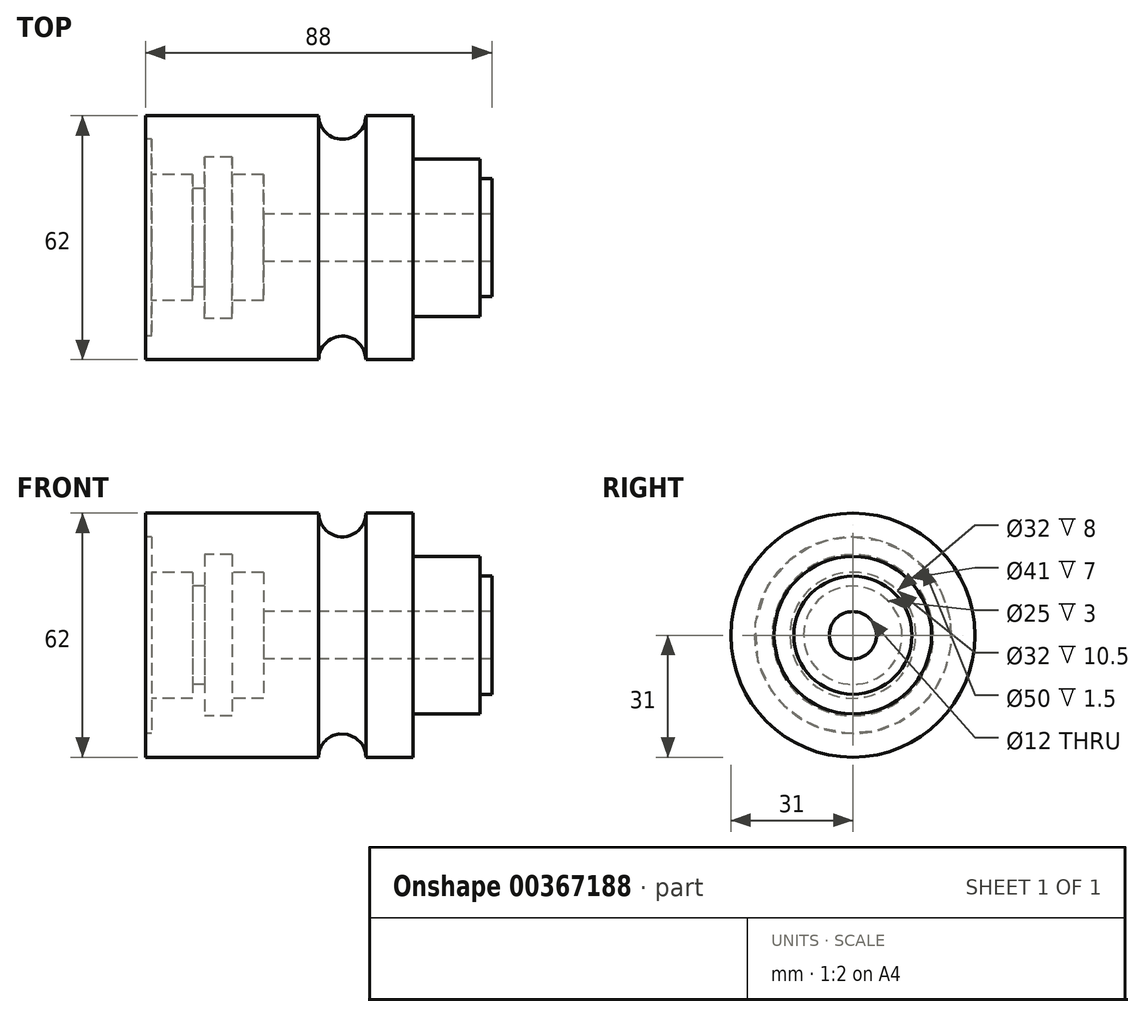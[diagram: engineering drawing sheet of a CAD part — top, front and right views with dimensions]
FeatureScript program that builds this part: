
annotation { "Feature Type Name" : "Feature", "Feature Type Description" : "" }
export const myFeature = defineFeature(function(context is Context, id is Id, definition is map)
    precondition{}
    {
        {
            var Q0;
            Q0=qCreatedBy(makeId("Front.planeOp"),FACE);
            var sketch = newSketch(context, id + "F0", { "sketchPlane" : qUnion([Q0])});
            skLineSegment(sketch, "E0", {"start": v(0, 0) * mm, "end": v(178.14, 0) * mm, "construction": true});
            skLineSegment(sketch, "E1", {"start": v(0, 0) * mm, "end": v(0, 31) * mm});
            skLineSegment(sketch, "E2", {"start": v(0, 31) * mm, "end": v(44, 31) * mm});
            skLineSegment(sketch, "E3", {"start": v(68, 31) * mm, "end": v(68, 20) * mm});
            skLineSegment(sketch, "E4", {"start": v(88, 15) * mm, "end": v(88, 0) * mm});
            skLineSegment(sketch, "E5", {"start": v(88, 0) * mm, "end": v(0, 0) * mm});
            skLineSegment(sketch, "E6", {"start": v(68, 20) * mm, "end": v(85, 20) * mm});
            skLineSegment(sketch, "E7", {"start": v(85, 20) * mm, "end": v(85, 15) * mm});
            skLineSegment(sketch, "E8", {"start": v(85, 15) * mm, "end": v(88, 15) * mm});
            skArc(sketch, "E9", {"start": v(44, 31) * mm, "mid": v(50, 25) * mm, "end": v(56, 31) * mm});
            skLineSegment(sketch, "E10.trimOffspring", {"start": v(56, 31) * mm, "end": v(68, 31) * mm});
            skSolve(sketch);
        }
        {
            var Q0;
            Q0=qSketchRegion(id+"F0",true);
            var Q1;
            Q1=sQuery(id+"F0.wireOp",EDGE,"E0");
            revolve(context, id + "F1", {"entities" : qUnion([Q0]), "axis" : qUnion([Q1]), "revolveType" : RevolveType.FULL});
        }
        {
            var Q0;
            Q0=qCreatedBy(makeId("Front.planeOp"),FACE);
            var sketch = newSketch(context, id + "F2", { "sketchPlane" : qUnion([Q0])});
            skLineSegment(sketch, "E11", {"start": v(0, 0) * mm, "end": v(0, 25) * mm});
            skLineSegment(sketch, "E12", {"start": v(0, 25) * mm, "end": v(1.5, 25) * mm});
            skLineSegment(sketch, "E13", {"start": v(1.5, 25) * mm, "end": v(1.5, 16) * mm});
            skLineSegment(sketch, "E14", {"start": v(1.5, 16) * mm, "end": v(12, 16) * mm});
            skLineSegment(sketch, "E15", {"start": v(12, 16) * mm, "end": v(12, 12.5) * mm});
            skLineSegment(sketch, "E16", {"start": v(12, 12.5) * mm, "end": v(15, 12.5) * mm});
            skLineSegment(sketch, "E17", {"start": v(22, 16) * mm, "end": v(30, 16) * mm});
            skLineSegment(sketch, "E18", {"start": v(30, 16) * mm, "end": v(30, 6) * mm});
            skLineSegment(sketch, "E19", {"start": v(30, 6) * mm, "end": v(88, 6) * mm});
            skLineSegment(sketch, "E20", {"start": v(88, 6) * mm, "end": v(88, 0) * mm});
            skLineSegment(sketch, "E21", {"start": v(88, 0) * mm, "end": v(0, 0) * mm});
            skLineSegment(sketch, "E22", {"start": v(0, 0) * mm, "end": v(-52.04, 0) * mm, "construction": true});
            skLineSegment(sketch, "E23", {"start": v(15, 12.5) * mm, "end": v(15, 20.5) * mm});
            skLineSegment(sketch, "E24", {"start": v(15, 20.5) * mm, "end": v(22, 20.5) * mm});
            skLineSegment(sketch, "E25", {"start": v(22, 20.5) * mm, "end": v(22, 16) * mm});
            skSolve(sketch);
        }
        {
            var Q0;
            Q0=qSketchRegion(id+"F2",true);
            var Q1;
            Q1=sQuery(id+"F2.wireOp",EDGE,"E22");
            revolve(context, id + "F3", {"operationType" : NewBodyOperationType.REMOVE, "entities" : qUnion([Q0]), "axis" : qUnion([Q1]), "revolveType" : RevolveType.FULL, "oppositeDirection" : true});
        }
    });
